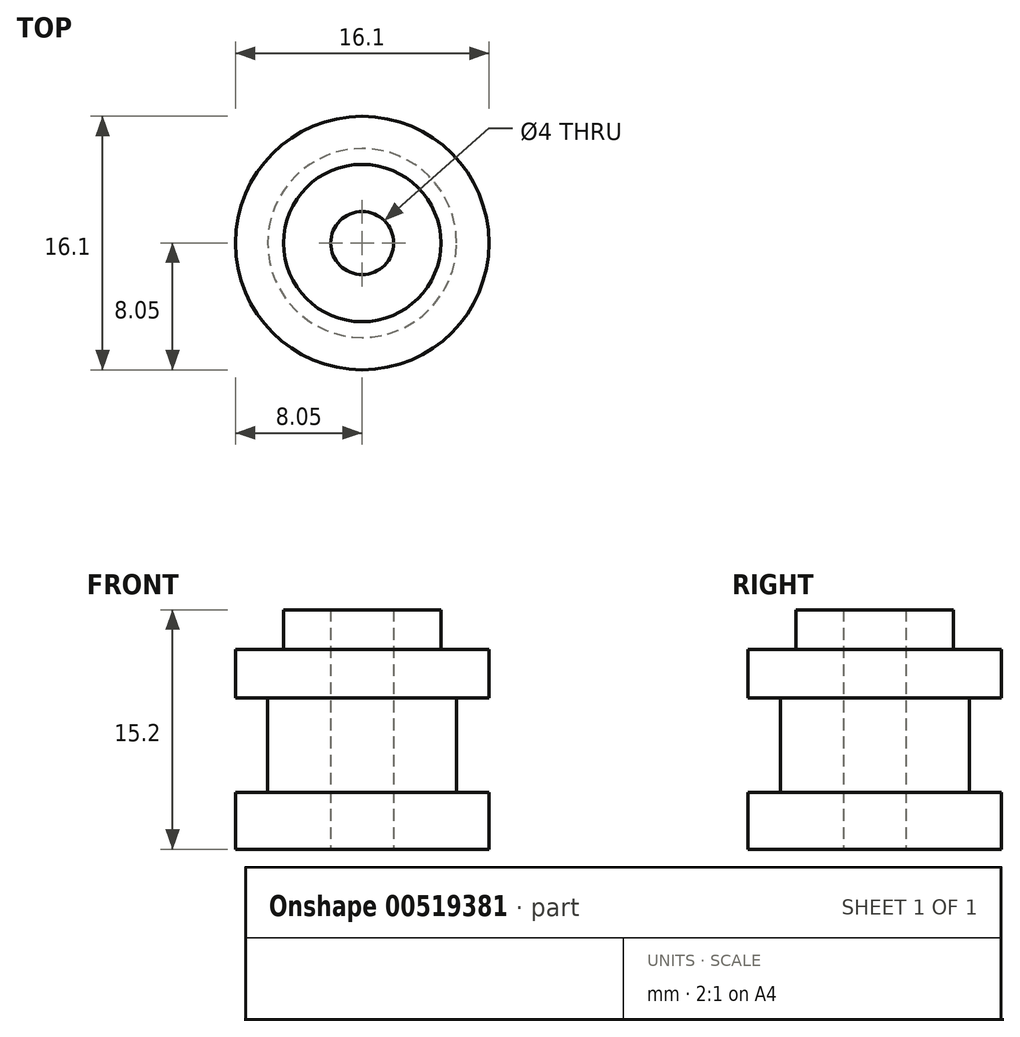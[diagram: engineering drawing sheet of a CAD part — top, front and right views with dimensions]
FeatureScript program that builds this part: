
annotation { "Feature Type Name" : "Feature", "Feature Type Description" : "" }
export const myFeature = defineFeature(function(context is Context, id is Id, definition is map)
    precondition{}
    {
        {
            var Q0;
            Q0=qCreatedBy(makeId("Top.planeOp"),FACE);
            var sketch = newSketch(context, id + "F0", { "sketchPlane" : qUnion([Q0])});
            skCircle(sketch, "E0", {"center": v(0, 0) * mm, "radius": 8.05 * mm});
            skSolve(sketch);
        }
        {
            var Q0;
            Q0 = qSketchRegion(id + "F0", true);
            extrude(context, id + "F1", {"entities" : qUnion([Q0]), "depth" : 3.6 * mm, "offsetDistance" : 25 * mm});
        }
        {
            var Q0;
            Q0=makeQuery(id+"F1.opExtrude","CAP_FACE",FACE,{"disambiguationData":[OSD([sQuery(id+"F0.wireOp",EDGE,"E0")])],"isStart":false});
            var sketch = newSketch(context, id + "F2", { "sketchPlane" : qUnion([Q0])});
            skCircle(sketch, "E1", {"center": v(0, 0) * mm, "radius": 6 * mm});
            skSolve(sketch);
        }
        {
            var Q0;
            Q0=makeQuery(id+"F2.imprint","IMPRINT",FACE,{"disambiguationData":[TD([[makeQuery(id+"F2.imprint","IMPRINT",EDGE,{"derivedFrom":sQuery(id+"F2.wireOp",EDGE,"E1")}),1.0]])]});
            extrude(context, id + "F3", {"entities" : qUnion([Q0]), "operationType" : NewBodyOperationType.ADD, "depth" : 6 * mm, "offsetDistance" : 25 * mm});
        }
        {
            var Q0;
            Q0=makeQuery(id+"F3.opExtrude","CAP_FACE",FACE,{"disambiguationData":[OSD([sQuery(id+"F2.wireOp",EDGE,"E1")])],"isStart":false});
            var sketch = newSketch(context, id + "F4", { "sketchPlane" : qUnion([Q0])});
            skCircle(sketch, "E2", {"center": v(0, 0) * mm, "radius": 8.05 * mm});
            skSolve(sketch);
        }
        {
            var Q0;
            Q0 = qSketchRegion(id + "F4", true);
            extrude(context, id + "F5", {"entities" : qUnion([Q0]), "operationType" : NewBodyOperationType.ADD, "depth" : 3.1 * mm, "offsetDistance" : 25 * mm});
        }
        {
            var Q0;
            Q0=makeQuery(id+"F5.opExtrude","CAP_FACE",FACE,{"disambiguationData":[OSD([sQuery(id+"F4.wireOp",EDGE,"E2")])],"isStart":false});
            var sketch = newSketch(context, id + "F6", { "sketchPlane" : qUnion([Q0])});
            skCircle(sketch, "E3", {"center": v(0, 0) * mm, "radius": 5 * mm});
            skSolve(sketch);
        }
        {
            var Q0;
            Q0 = qSketchRegion(id + "F6", true);
            extrude(context, id + "F7", {"entities" : qUnion([Q0]), "operationType" : NewBodyOperationType.ADD, "depth" : 2.5 * mm, "offsetDistance" : 25 * mm});
        }
        {
            var Q0;
            Q0=makeQuery(id+"F1.opExtrude","CAP_FACE",FACE,{"disambiguationData":[OSD([sQuery(id+"F0.wireOp",EDGE,"E0")])],"isStart":true});
            var sketch = newSketch(context, id + "F8", { "sketchPlane" : qUnion([Q0])});
            skCircle(sketch, "E4", {"center": v(0, 0) * mm, "radius": 2 * mm});
            skSolve(sketch);
        }
        {
            var Q0;
            Q0 = qSketchRegion(id + "F8", true);
            extrude(context, id + "F9", {"entities" : qUnion([Q0]), "operationType" : NewBodyOperationType.REMOVE, "endBound" : BoundingType.THROUGH_ALL, "oppositeDirection" : true, "depth" : 25 * mm, "offsetDistance" : 25 * mm});
        }
    });
